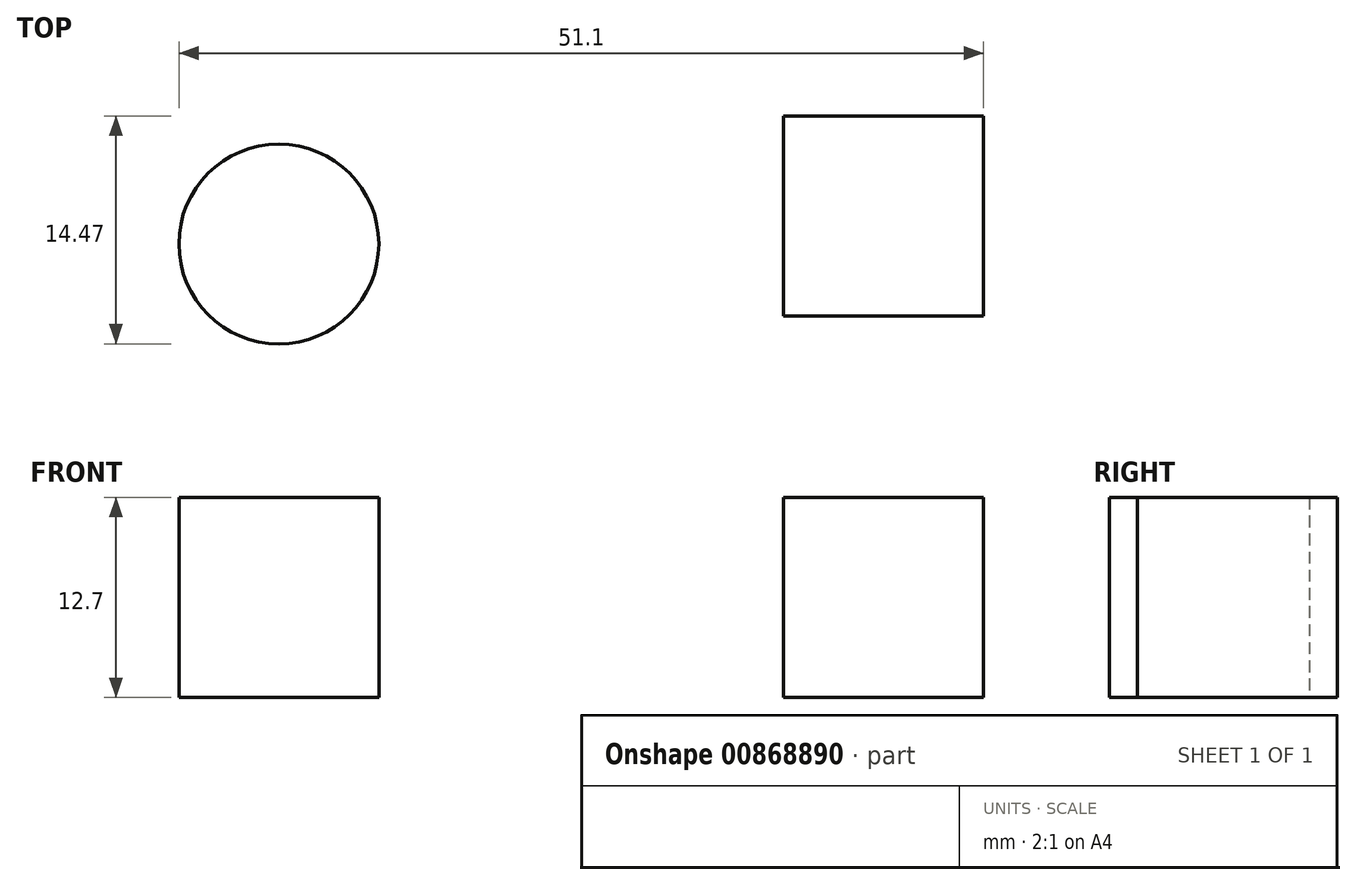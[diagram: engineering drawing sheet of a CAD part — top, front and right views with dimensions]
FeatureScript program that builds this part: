
annotation { "Feature Type Name" : "Feature", "Feature Type Description" : "" }
export const myFeature = defineFeature(function(context is Context, id is Id, definition is map)
    precondition{}
    {
        {
            var Q0;
            Q0=qCreatedBy(makeId("Top.planeOp"),FACE);
            var sketch = newSketch(context, id + "F0", { "sketchPlane" : qUnion([Q0])});
            skCircle(sketch, "E0", {"center": v(-25.42, 12.17) * mm, "radius": 6.35 * mm});
            skLineSegment(sketch, "E1.bottom", {"start": v(6.63, 20.3) * mm, "end": v(19.33, 20.3) * mm});
            skLineSegment(sketch, "E1.top", {"start": v(6.63, 7.6) * mm, "end": v(19.33, 7.6) * mm});
            skLineSegment(sketch, "E1.left", {"start": v(6.63, 20.3) * mm, "end": v(6.63, 7.6) * mm});
            skLineSegment(sketch, "E1.right", {"start": v(19.33, 20.3) * mm, "end": v(19.33, 7.6) * mm});
            skSolve(sketch);
        }
        {
            var Q0;
            Q0=makeQuery(id+"F0.imprint","IMPRINT",FACE,{"disambiguationData":[TD([[makeQuery(id+"F0.imprint","IMPRINT",EDGE,{"derivedFrom":sQuery(id+"F0.wireOp",EDGE,"E0")}),1.0]])]});
            var Q1;
            Q1=makeQuery(id+"F0.imprint","IMPRINT",FACE,{"disambiguationData":[TD([[makeQuery(id+"F0.imprint","IMPRINT",EDGE,{"derivedFrom":sQuery(id+"F0.wireOp",EDGE,"E1.bottom")}),-1.0]])]});
            extrude(context, id + "F1", {"entities" : qUnion([Q0, Q1]), "depth" : 12.7 * mm, "offsetDistance" : 25.4 * mm});
        }
    });
